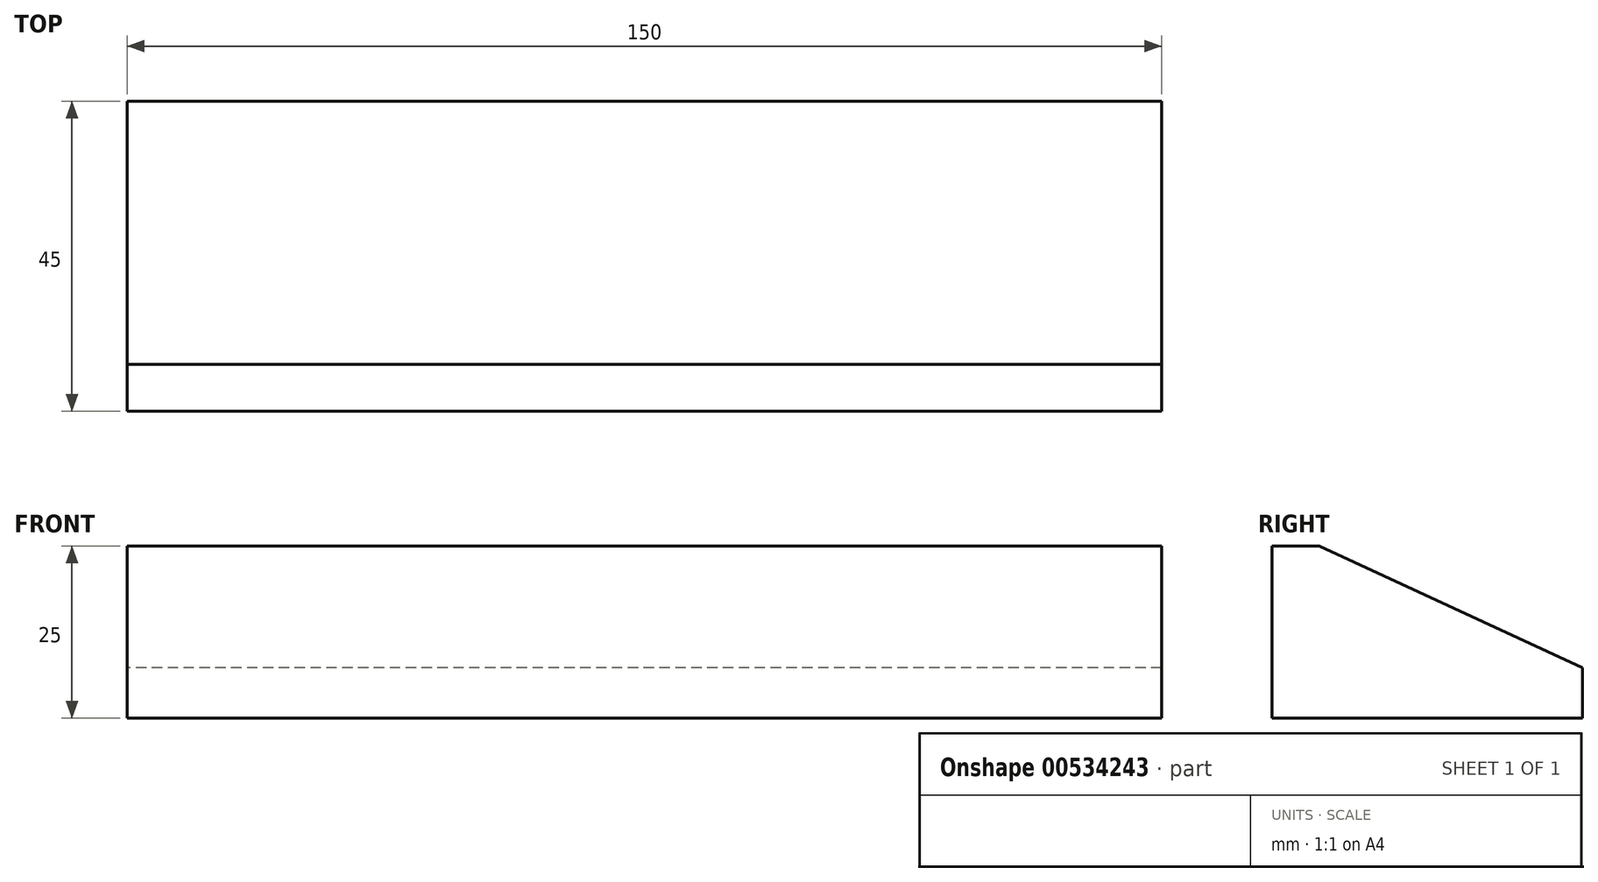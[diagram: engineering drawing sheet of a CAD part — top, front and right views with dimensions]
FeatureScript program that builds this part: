
annotation { "Feature Type Name" : "Feature", "Feature Type Description" : "" }
export const myFeature = defineFeature(function(context is Context, id is Id, definition is map)
    precondition{}
    {
        {
            var Q0;
            Q0=qCreatedBy(makeId("Right.planeOp"),FACE);
            var sketch = newSketch(context, id + "F0", { "sketchPlane" : qUnion([Q0])});
            skLineSegment(sketch, "E0.bottom", {"start": v(0, 0) * mm, "end": v(45, 0) * mm});
            skLineSegment(sketch, "E0.top", {"start": v(0, 25) * mm, "end": v(6.84, 25) * mm});
            skLineSegment(sketch, "E0.left", {"start": v(0, 0) * mm, "end": v(0, 25) * mm});
            skLineSegment(sketch, "E0.right", {"start": v(45, 0) * mm, "end": v(45, 7.33) * mm});
            skLineSegment(sketch, "E1", {"start": v(6.84, 25) * mm, "end": v(45, 7.33) * mm});
            skSolve(sketch);
        }
        {
            var Q0;
            Q0 = qSketchRegion(id + "F0", true);
            extrude(context, id + "F1", {"entities" : qUnion([Q0]), "depth" : 150 * mm, "offsetDistance" : 25 * mm});
        }
    });
